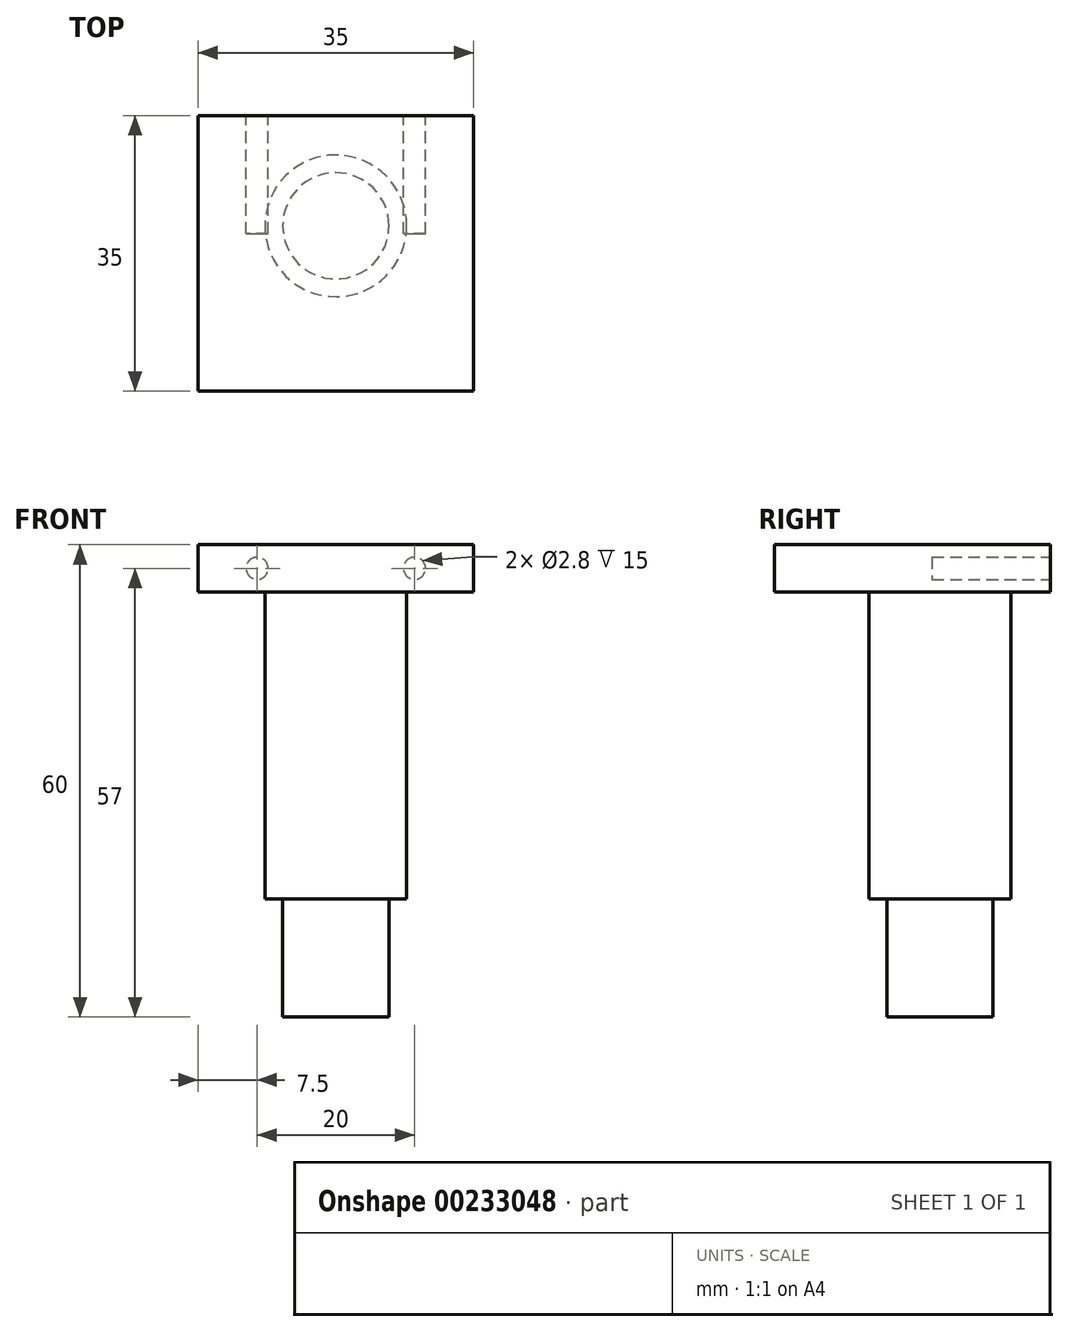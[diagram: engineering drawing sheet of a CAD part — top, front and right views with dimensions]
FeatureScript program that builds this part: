
annotation { "Feature Type Name" : "Feature", "Feature Type Description" : "" }
export const myFeature = defineFeature(function(context is Context, id is Id, definition is map)
    precondition{}
    {
        {
            var Q0;
            Q0=qCreatedBy(makeId("Top.planeOp"),FACE);
            cPlane(context, id + "F0", {"entities" : qUnion([Q0]), "cplaneType" : CPlaneType.OFFSET, "offset" : 40 * mm, "width" : 150 * mm, "height" : 150 * mm});
        }
        {
            var Q0;
            Q0=qCreatedBy(id+"F0.planeOp",FACE);
            var sketch = newSketch(context, id + "F1", { "sketchPlane" : qUnion([Q0])});
            skCircle(sketch, "E0", {"center": v(0, 0) * mm, "radius": 6.75 * mm});
            skSolve(sketch);
        }
        {
            var Q0;
            Q0=makeQuery(id+"F1.imprint","IMPRINT",FACE,{"disambiguationData":[TD([[makeQuery(id+"F1.imprint","IMPRINT",EDGE,{"derivedFrom":sQuery(id+"F1.wireOp",EDGE,"E0")}),1.0]])]});
            extrude(context, id + "F2", {"entities" : qUnion([Q0]), "oppositeDirection" : true, "depth" : 15 * mm});
        }
        {
            var Q0;
            Q0=qCreatedBy(id+"F0.planeOp",FACE);
            var sketch = newSketch(context, id + "F3", { "sketchPlane" : qUnion([Q0])});
            skCircle(sketch, "E1", {"center": v(0, 0) * mm, "radius": 9 * mm});
            skSolve(sketch);
        }
        {
            var Q0;
            Q0=makeQuery(id+"F3.imprint","IMPRINT",FACE,{"disambiguationData":[TD([[makeQuery(id+"F3.imprint","IMPRINT",EDGE,{"derivedFrom":sQuery(id+"F3.wireOp",EDGE,"E1")}),1.0]])]});
            extrude(context, id + "F4", {"entities" : qUnion([Q0]), "operationType" : NewBodyOperationType.ADD, "depth" : 45 * mm});
        }
        {
            var Q0;
            Q0=makeQuery(id+"F4.opExtrude","CAP_FACE",FACE,{"disambiguationData":[OSD([sQuery(id+"F3.wireOp",EDGE,"E1")])],"isStart":false});
            var sketch = newSketch(context, id + "F5", { "sketchPlane" : qUnion([Q0])});
            skLineSegment(sketch, "E2.bottom", {"start": v(-17.5, 14) * mm, "end": v(17.5, 14) * mm});
            skLineSegment(sketch, "E2.top", {"start": v(-17.5, -21) * mm, "end": v(17.5, -21) * mm});
            skLineSegment(sketch, "E2.left", {"start": v(-17.5, 14) * mm, "end": v(-17.5, -21) * mm});
            skLineSegment(sketch, "E2.right", {"start": v(17.5, 14) * mm, "end": v(17.5, -21) * mm});
            skSolve(sketch);
        }
        {
            var Q0;
            Q0=makeQuery(id+"F5.imprint","IMPRINT",FACE,{"disambiguationData":[TD([[makeQuery(id+"F5.imprint","IMPRINT",EDGE,{"derivedFrom":sQuery(id+"F5.wireOp",EDGE,"E2.bottom")}),-1.0]])]});
            extrude(context, id + "F6", {"entities" : qUnion([Q0]), "operationType" : NewBodyOperationType.ADD, "oppositeDirection" : true, "depth" : 6 * mm});
        }
        {
            var Q0;
            Q0=makeQuery(id+"F6.opExtrude","SWEPT_FACE",FACE,{"disambiguationData":[OSD([sQuery(id+"F5.wireOp",EDGE,"E2.bottom")])]});
            var sketch = newSketch(context, id + "F7", { "sketchPlane" : qUnion([Q0])});
            skCircle(sketch, "E3", {"center": v(-10, 82) * mm, "radius": 1.4 * mm});
            skCircle(sketch, "E4", {"center": v(10, 82) * mm, "radius": 1.4 * mm});
            skSolve(sketch);
        }
        {
            var Q0;
            Q0=makeQuery(id+"F7.imprint","IMPRINT",FACE,{"disambiguationData":[TD([[makeQuery(id+"F7.imprint","IMPRINT",EDGE,{"derivedFrom":sQuery(id+"F7.wireOp",EDGE,"E3")}),1.0]])]});
            var Q1;
            Q1=makeQuery(id+"F7.imprint","IMPRINT",FACE,{"disambiguationData":[TD([[makeQuery(id+"F7.imprint","IMPRINT",EDGE,{"derivedFrom":sQuery(id+"F7.wireOp",EDGE,"E4")}),1.0]])]});
            extrude(context, id + "F8", {"entities" : qUnion([Q0, Q1]), "operationType" : NewBodyOperationType.REMOVE, "oppositeDirection" : true, "depth" : 15 * mm});
        }
    });
